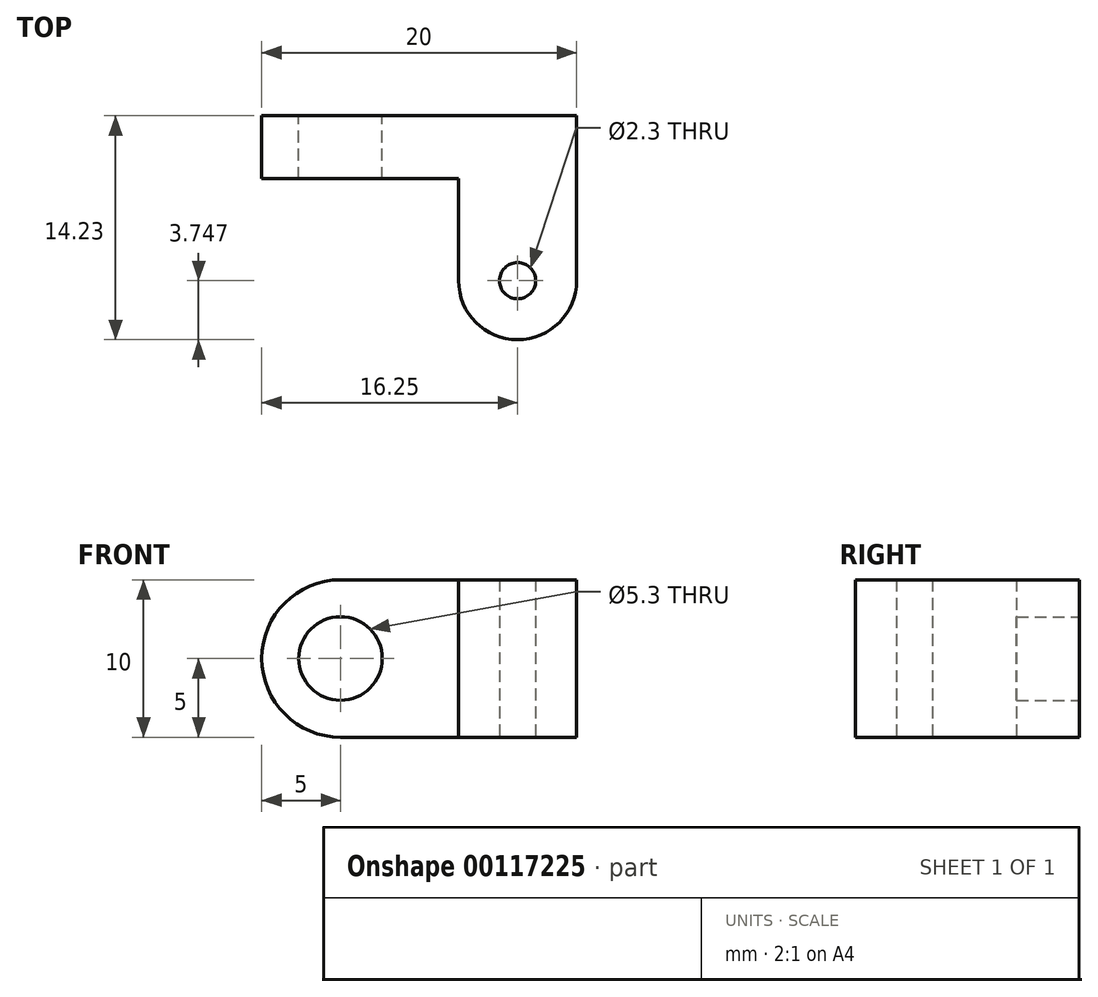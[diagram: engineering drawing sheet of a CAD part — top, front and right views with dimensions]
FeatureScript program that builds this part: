
annotation { "Feature Type Name" : "Feature", "Feature Type Description" : "" }
export const myFeature = defineFeature(function(context is Context, id is Id, definition is map)
    precondition{}
    {
        {
            var Q0;
            Q0=qCreatedBy(makeId("Front.planeOp"),FACE);
            var sketch = newSketch(context, id + "F0", { "sketchPlane" : qUnion([Q0])});
            skLineSegment(sketch, "E0.bottom", {"start": v(7.5, -5) * mm, "end": v(-7.5, -5) * mm});
            skLineSegment(sketch, "E0.top", {"start": v(7.5, 5) * mm, "end": v(-7.5, 5) * mm});
            skLineSegment(sketch, "E0.left", {"start": v(7.5, -5) * mm, "end": v(7.5, 5) * mm});
            skPoint(sketch, "E0.middle", {"position": v(0, 0) * mm});
            skArc(sketch, "E1", {"start": v(-7.5, 5) * mm, "mid": v(-12.5, 0) * mm, "end": v(-7.5, -5) * mm});
            skCircle(sketch, "E2", {"center": v(-7.5, 0) * mm, "radius": 2.65 * mm});
            skSolve(sketch);
        }
        {
            var Q0;
            Q0=makeQuery(id+"F0.imprint","IMPRINT",FACE,{"disambiguationData":[TD([[makeQuery(id+"F0.imprint","IMPRINT",EDGE,{"derivedFrom":sQuery(id+"F0.wireOp",EDGE,"E0.bottom")}),-1.0]])]});
            extrude(context, id + "F1", {"entities" : qUnion([Q0]), "depth" : 4 * mm});
        }
        {
            var Q0;
            Q0=makeQuery(id+"F1.opExtrude","SWEPT_FACE",FACE,{"disambiguationData":[OSD([sQuery(id+"F0.wireOp",EDGE,"E0.bottom")])]});
            var sketch = newSketch(context, id + "F2", { "sketchPlane" : qUnion([Q0])});
            skLineSegment(sketch, "E3.bottom", {"start": v(7.5, 4) * mm, "end": v(0, 4) * mm});
            skLineSegment(sketch, "E3.left", {"start": v(7.5, 4) * mm, "end": v(7.5, 10.48) * mm});
            skLineSegment(sketch, "E3.right", {"start": v(0, 4) * mm, "end": v(0, 10.48) * mm});
            skArc(sketch, "E4", {"start": v(7.5, 10.48) * mm, "mid": v(3.75, 14.23) * mm, "end": v(0, 10.48) * mm});
            skCircle(sketch, "E5", {"center": v(3.75, 10.48) * mm, "radius": 1.15 * mm});
            skSolve(sketch);
        }
        {
            var Q0;
            Q0=makeQuery(id+"F2.imprint","IMPRINT",FACE,{"disambiguationData":[TD([[makeQuery(id+"F2.imprint","IMPRINT",EDGE,{"derivedFrom":sQuery(id+"F2.wireOp",EDGE,"E3.bottom")}),-1.0]])]});
            var Q1;
            Q1=makeQuery(id+"F1.opExtrude","SWEPT_FACE",FACE,{"disambiguationData":[OSD([sQuery(id+"F0.wireOp",EDGE,"E0.top")])]});
            extrude(context, id + "F3", {"entities" : qUnion([Q0]), "operationType" : NewBodyOperationType.ADD, "endBound" : BoundingType.UP_TO_SURFACE, "oppositeDirection" : true, "endBoundEntityFace" : qUnion([Q1]), "depth" : 25 * mm});
        }
    });
